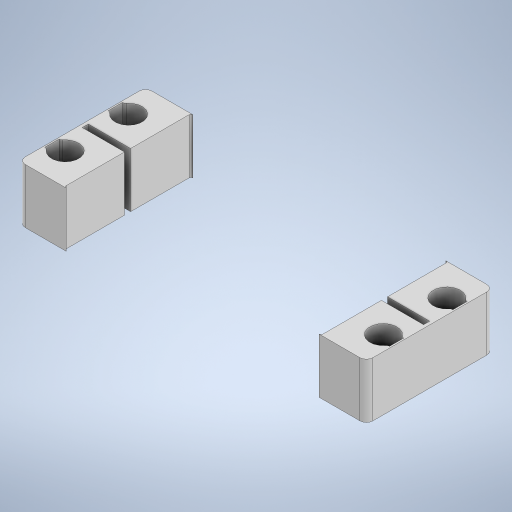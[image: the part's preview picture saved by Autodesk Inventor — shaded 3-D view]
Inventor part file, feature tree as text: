
AUTODESK INVENTOR PART (.ipt)
format: ipt  version: 2024 (Build 280153000, 153)  size: 480,768 bytes
history: native  units: mm
features: other x4, plane x2, reference x2, sketch x1, extrude x1
ambient origin geometry x8: Origin, YZ Plane, XZ Plane, XY Plane, X Axis, Y Axis, Z Axis, Center Point
bodies: Solid1 (feature_tree)
feature tree (10):
  plane  "Work Plane1"
  sketch  "Sketch2"  dims[d0=10.0mm d1=0.0mm]
  plane  "Work Plane2"
  extrude  "Extrusion1"  [1 undecoded]
  reference  "Reference3"
  reference  "Reference4"
  other  "<userpath> windows\Documents\Inventor\Robotska_roka\roka.iam"
  other  "roka.iam"
  other  "Servo Motor MG996R  With Attachments:7"
  other  "servoMotorMG996R_7"
note: 1 required parameter value undecoded (feature->parameter linkage not recoverable at this tier; creation-order binding heuristic only, values carry confidence <= 0.55)
